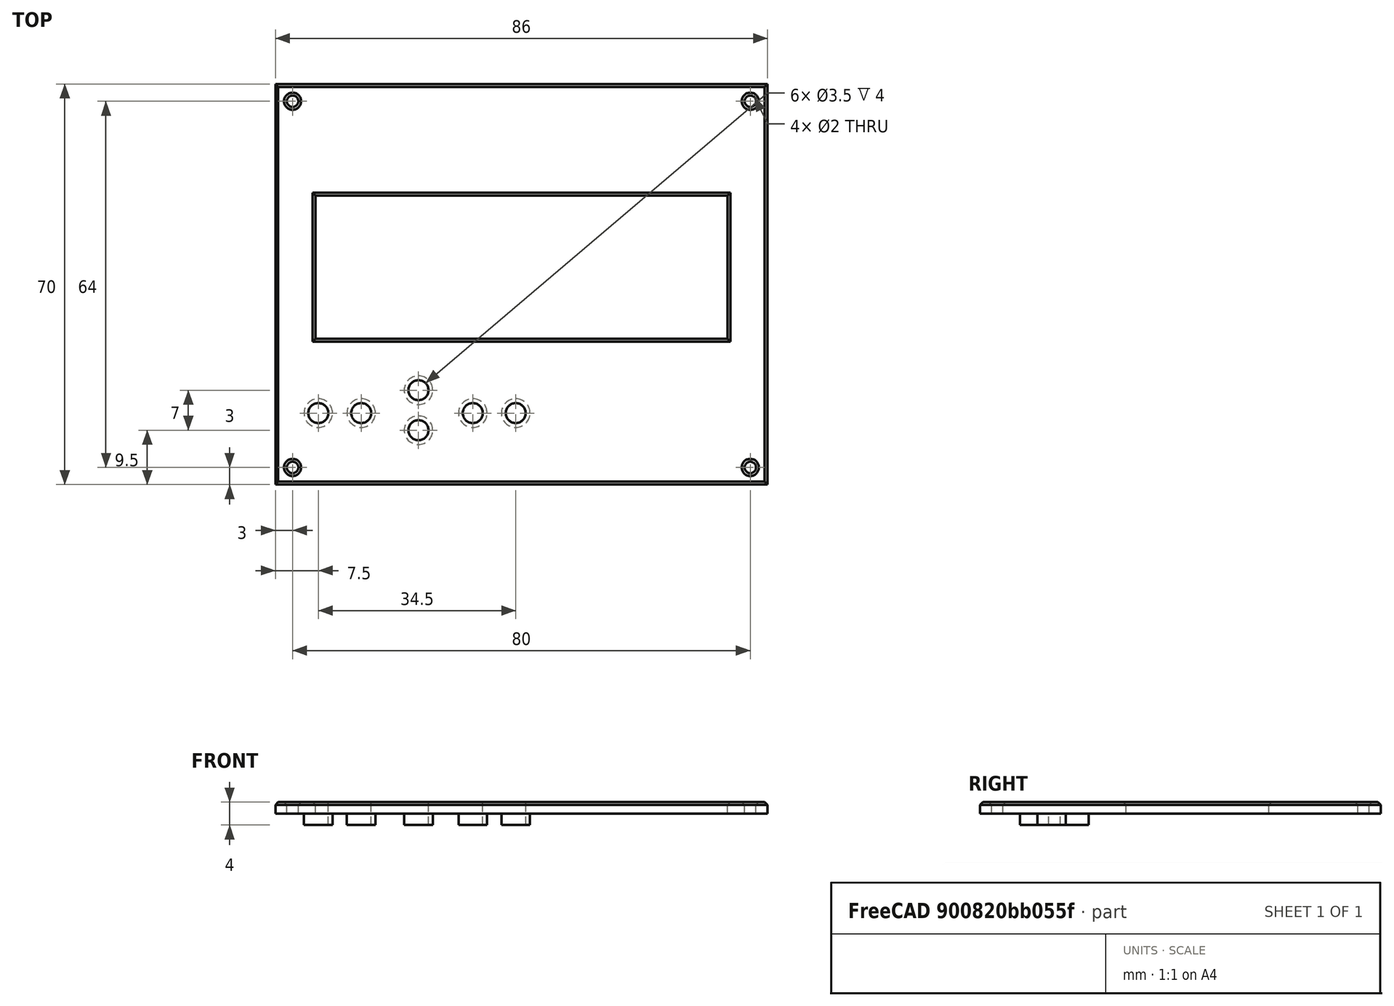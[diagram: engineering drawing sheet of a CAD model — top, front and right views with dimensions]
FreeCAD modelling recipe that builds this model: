
FCSTD DOCUMENT  (FreeCAD 0.19RUnknown)
Label: caja_tapa_01
License: All rights reserved
LicenseURL: http://en.wikipedia.org/wiki/All_rights_reserved
objects: Part::Cut×17, Part::Cylinder×16, Part::Box×2, Part::Chamfer×2, Part::MultiFuse×1, Part::Refine×1
note: 39 computed .brp shape members not serialized (recipe doc carries the construction recipe); baked Part::Feature solids carry a one-line shape summary decoded from their .brp

FEATURE [Part::Box] Box  label="Cubo"
  AttacherType = Attacher::AttachEngine3D
  Height = 2
  Length = 86
  Width = 70
FEATURE [Part::Box] Box001  label="Cubo001"
  AttacherType = Attacher::AttachEngine3D
  Height = 10
  Length = 72
  Placement = pos=(7,25.5,0) rot=(0,0,1;0rad)
  Width = 25
FEATURE [Part::Cut] Cut
  Base = -> Box
  Tool = -> Box001
FEATURE [Part::Cylinder] Cylinder  label="Cilindro"
  Angle = 360
  AttacherType = Attacher::AttachEngine3D
  Height = 10
  Placement = pos=(3,3,-1) rot=(0,0,1;0rad)
  Radius = 1
FEATURE [Part::Cylinder] Cylinder001  label="Cilindro001"
  Angle = 360
  AttacherType = Attacher::AttachEngine3D
  Height = 10
  Placement = pos=(3,67,-1) rot=(0,0,1;0rad)
  Radius = 1
FEATURE [Part::Cylinder] Cylinder002  label="Cilindro002"
  Angle = 360
  AttacherType = Attacher::AttachEngine3D
  Height = 10
  Placement = pos=(83,3,-1) rot=(0,0,1;0rad)
  Radius = 1
FEATURE [Part::Cylinder] Cylinder003  label="Cilindro003"
  Angle = 360
  AttacherType = Attacher::AttachEngine3D
  Height = 10
  Placement = pos=(83,67,-1) rot=(0,0,1;0rad)
  Radius = 1
FEATURE [Part::Cylinder] Cylinder004  label="Cilindro004"
  Angle = 360
  AttacherType = Attacher::AttachEngine3D
  Height = 10
  Placement = pos=(7.5,12.5,-3) rot=(0,0,1;0rad)
  Radius = 1.75
FEATURE [Part::Cylinder] Cylinder005  label="Cilindro005"
  Angle = 360
  AttacherType = Attacher::AttachEngine3D
  Height = 10
  Placement = pos=(15,12.5,-3) rot=(0,0,1;0rad)
  Radius = 1.75
FEATURE [Part::Cylinder] Cylinder006  label="Cilindro006"
  Angle = 360
  AttacherType = Attacher::AttachEngine3D
  Height = 10
  Placement = pos=(25,16.5,-3) rot=(0,0,1;0rad)
  Radius = 1.75
FEATURE [Part::Cylinder] Cylinder007  label="Cilindro007"
  Angle = 360
  AttacherType = Attacher::AttachEngine3D
  Height = 10
  Placement = pos=(25,9.5,-3) rot=(0,0,1;0rad)
  Radius = 1.75
FEATURE [Part::Cylinder] Cylinder008  label="Cilindro008"
  Angle = 360
  AttacherType = Attacher::AttachEngine3D
  Height = 10
  Placement = pos=(34.5,12.5,-3) rot=(0,0,1;0rad)
  Radius = 1.75
FEATURE [Part::Cylinder] Cylinder009  label="Cilindro009"
  Angle = 360
  AttacherType = Attacher::AttachEngine3D
  Height = 10
  Placement = pos=(42,12.5,-3) rot=(0,0,1;0rad)
  Radius = 1.75
FEATURE [Part::Cut] Cut001
  Base = -> Cut
  Tool = -> Cylinder
FEATURE [Part::Cut] Cut002
  Base = -> Cut001
  Tool = -> Cylinder001
FEATURE [Part::Cut] Cut003
  Base = -> Cut002
  Tool = -> Cylinder002
FEATURE [Part::Cut] Cut004
  Base = -> Cut003
  Tool = -> Cylinder003
FEATURE [Part::Cut] Cut005
  Base = -> Cut004
  Tool = -> Cylinder004
FEATURE [Part::Cut] Cut006
  Base = -> Cut005
  Tool = -> Cylinder005
FEATURE [Part::Cut] Cut007
  Base = -> Cut006
  Tool = -> Cylinder006
FEATURE [Part::Cut] Cut008
  Base = -> Cut007
  Tool = -> Cylinder007
FEATURE [Part::Cut] Cut009
  Base = -> Cut008
  Tool = -> Cylinder008
FEATURE [Part::Cut] Cut010
  Base = -> Cut009
  Tool = -> Cylinder009
FEATURE [Part::Chamfer] Chamfer
  Base = -> Cut010
  Edges = 8 edges r=0.5: [Edge2,Edge7,Edge8,Edge9,Edge19,Edge20,Edge21,Edge22]
FEATURE [Part::Chamfer] Chamfer001
  Base = -> Chamfer
  Edges = 4 edges r=0.5: [Edge34,Edge41,Edge42,Edge43]
FEATURE [Part::Cylinder] Cylinder010  label="Cilindro010"
  Angle = 360
  AttacherType = Attacher::AttachEngine3D
  Height = 4
  Placement = pos=(42,12.5,-2) rot=(0,0,1;0rad)
  Radius = 2.5
FEATURE [Part::Cylinder] Cylinder011  label="Cilindro011"
  Angle = 360
  AttacherType = Attacher::AttachEngine3D
  Height = 4
  Placement = pos=(34.5,12.5,-2) rot=(0,0,1;0rad)
  Radius = 2.5
FEATURE [Part::Cylinder] Cylinder012  label="Cilindro012"
  Angle = 360
  AttacherType = Attacher::AttachEngine3D
  Height = 4
  Placement = pos=(25,16.5,-2) rot=(0,0,1;0rad)
  Radius = 2.5
FEATURE [Part::Cylinder] Cylinder013  label="Cilindro013"
  Angle = 360
  AttacherType = Attacher::AttachEngine3D
  Height = 4
  Placement = pos=(25,9.5,-2) rot=(0,0,1;0rad)
  Radius = 2.5
FEATURE [Part::Cylinder] Cylinder014  label="Cilindro014"
  Angle = 360
  AttacherType = Attacher::AttachEngine3D
  Height = 4
  Placement = pos=(15,12.5,-2) rot=(0,0,1;0rad)
  Radius = 2.5
FEATURE [Part::Cylinder] Cylinder015  label="Cilindro015"
  Angle = 360
  AttacherType = Attacher::AttachEngine3D
  Height = 4
  Placement = pos=(7.5,12.5,-2) rot=(0,0,1;0rad)
  Radius = 2.5
FEATURE [Part::Cut] Cut011
  Base = -> Cylinder010
  Tool = -> Cylinder009
FEATURE [Part::Cut] Cut012
  Base = -> Cylinder011
  Tool = -> Cylinder008
FEATURE [Part::Cut] Cut013
  Base = -> Cylinder013
  Tool = -> Cylinder007
FEATURE [Part::Cut] Cut014
  Base = -> Cylinder012
  Tool = -> Cylinder006
FEATURE [Part::Cut] Cut015
  Base = -> Cylinder014
  Tool = -> Cylinder005
FEATURE [Part::Cut] Cut016
  Base = -> Cylinder015
  Tool = -> Cylinder004
FEATURE [Part::MultiFuse] Fusion
  Shapes = -> [Chamfer001,Cut011,Cut012,Cut013,Cut014,Cut015,Cut016]
FEATURE [Part::Refine] Fusion001
  Source = -> Fusion
